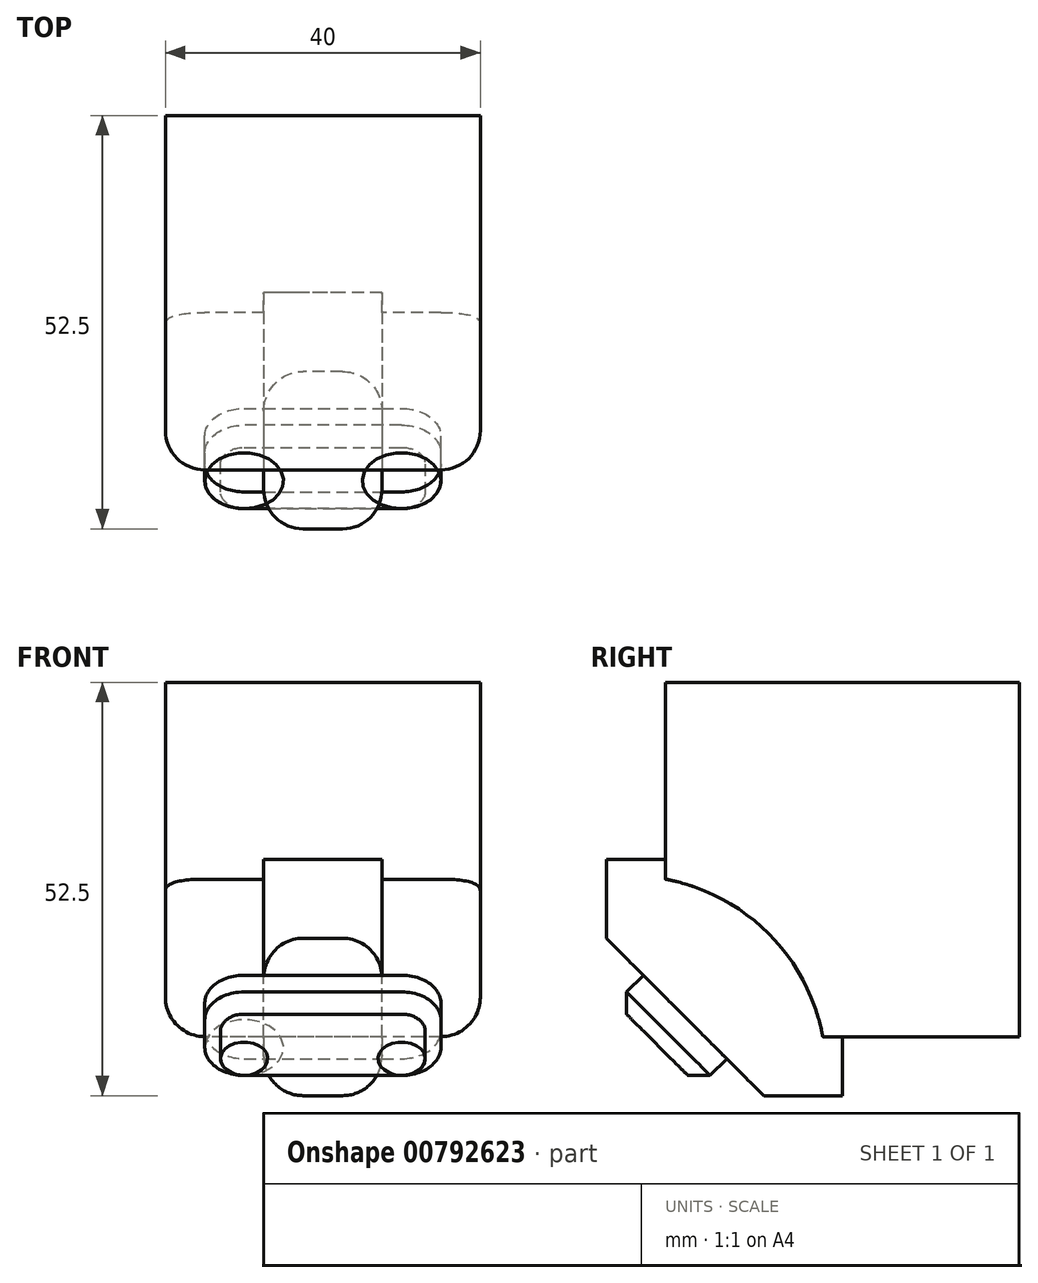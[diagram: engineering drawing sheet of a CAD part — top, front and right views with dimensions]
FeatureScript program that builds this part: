
annotation { "Feature Type Name" : "Feature", "Feature Type Description" : "" }
export const myFeature = defineFeature(function(context is Context, id is Id, definition is map)
    precondition{}
    {
        {
            var Q0;
            Q0=qCreatedBy(makeId("Top.planeOp"),FACE);
            var sketch = newSketch(context, id + "F0", { "sketchPlane" : qUnion([Q0])});
            skLineSegment(sketch, "E0.bottom", {"start": v(20, -22.5) * mm, "end": v(-20, -22.5) * mm});
            skLineSegment(sketch, "E0.top", {"start": v(20, 22.5) * mm, "end": v(-20, 22.5) * mm});
            skLineSegment(sketch, "E0.left", {"start": v(20, -22.5) * mm, "end": v(20, 22.5) * mm});
            skLineSegment(sketch, "E0.right", {"start": v(-20, -22.5) * mm, "end": v(-20, 22.5) * mm});
            skPoint(sketch, "E0.middle", {"position": v(0, 0) * mm});
            skSolve(sketch);
        }
        {
            var Q0;
            Q0=makeQuery(id+"F0.imprint","IMPRINT",FACE,{"disambiguationData":[TD([[makeQuery(id+"F0.imprint","IMPRINT",EDGE,{"derivedFrom":sQuery(id+"F0.wireOp",EDGE,"E0.bottom")}),-1.0]])]});
            extrude(context, id + "F1", {"entities" : qUnion([Q0]), "endBound" : BoundingType.SYMMETRIC, "depth" : 45 * mm, "offsetDistance" : 25 * mm});
        }
        {
            var Q0;
            Q0=makeQuery(id+"F1.opExtrude","SWEPT_FACE",FACE,{"disambiguationData":[OSD([sQuery(id+"F0.wireOp",EDGE,"E0.right")])]});
            var sketch = newSketch(context, id + "F2", { "sketchPlane" : qUnion([Q0])});
            skLineSegment(sketch, "E1", {"start": v(22.5, -22.5) * mm, "end": v(2.5, -22.5) * mm});
            skLineSegment(sketch, "E2", {"start": v(22.5, -22.5) * mm, "end": v(22.5, -2.5) * mm});
            skArc(sketch, "E3", {"start": v(22.5, -2.5) * mm, "mid": v(9.4, -9.4) * mm, "end": v(2.5, -22.5) * mm});
            skSolve(sketch);
        }
        {
            var Q0;
            Q0 = qSketchRegion(id + "F2", true);
            extrude(context, id + "F3", {"entities" : qUnion([Q0]), "operationType" : NewBodyOperationType.REMOVE, "endBound" : BoundingType.THROUGH_ALL, "oppositeDirection" : true, "depth" : 25 * mm, "offsetDistance" : 25 * mm});
        }
        {
            var Q0;
            Q0=qCreatedBy(makeId("Right.planeOp"),FACE);
            var sketch = newSketch(context, id + "F4", { "sketchPlane" : qUnion([Q0])});
            skLineSegment(sketch, "E4", {"start": v(0, 0) * mm, "end": v(-30, 0) * mm});
            skLineSegment(sketch, "E5", {"start": v(0, 0) * mm, "end": v(0, -30) * mm});
            skLineSegment(sketch, "E6", {"start": v(0, -30) * mm, "end": v(-10, -30) * mm});
            skLineSegment(sketch, "E7", {"start": v(-30, 0) * mm, "end": v(-30, -10) * mm});
            skLineSegment(sketch, "E8", {"start": v(-10, -30) * mm, "end": v(-30, -10) * mm});
            skSolve(sketch);
        }
        {
            var Q0;
            Q0 = qSketchRegion(id + "F4", true);
            extrude(context, id + "F5", {"entities" : qUnion([Q0]), "operationType" : NewBodyOperationType.ADD, "endBound" : BoundingType.SYMMETRIC, "depth" : 15 * mm, "offsetDistance" : 25 * mm});
        }
        {
            var Q0;
            Q0=makeQuery(id+"F1.opExtrude","SWEPT_EDGE",EDGE,{"disambiguationData":[OSD([sQuery(id+"F0.wireOp",EDGE,"E0.bottom"),sQuery(id+"F0.wireOp",EDGE,"E0.right")])]});
            var Q1;
            Q1=makeQuery(id+"F1.opExtrude","SWEPT_EDGE",EDGE,{"disambiguationData":[OSD([sQuery(id+"F0.wireOp",EDGE,"E0.bottom"),sQuery(id+"F0.wireOp",EDGE,"E0.left")])]});
            var Q2;
            Q2=makeQuery(id+"F1.opExtrude","CAP_EDGE",EDGE,{"disambiguationData":[OSD([sQuery(id+"F0.wireOp",EDGE,"E0.right")])],"isStart":true});
            var Q3;
            Q3=makeQuery(id+"F1.opExtrude","CAP_EDGE",EDGE,{"disambiguationData":[OSD([sQuery(id+"F0.wireOp",EDGE,"E0.left")])],"isStart":true});
            var Q4;
            Q4=makeQuery(id+"F5.opExtrude","CAP_EDGE",EDGE,{"disambiguationData":[OSD([sQuery(id+"F4.wireOp",EDGE,"E7")])],"isStart":false});
            var Q5;
            Q5=makeQuery(id+"F5.opExtrude","CAP_EDGE",EDGE,{"disambiguationData":[OSD([sQuery(id+"F4.wireOp",EDGE,"E7")])],"isStart":true});
            var Q6;
            Q6=makeQuery(id+"F5.opExtrude","CAP_EDGE",EDGE,{"disambiguationData":[OSD([sQuery(id+"F4.wireOp",EDGE,"E6")])],"isStart":false});
            var Q7;
            Q7=makeQuery(id+"F5.opExtrude","CAP_EDGE",EDGE,{"disambiguationData":[OSD([sQuery(id+"F4.wireOp",EDGE,"E6")])],"isStart":true});
            fillet(context, id + "F6", {"entities" : qUnion([Q0, Q1, Q2, Q3, Q4, Q5, Q6, Q7]), "radius" : 5 * mm, "tangentPropagation" : true, "allowEdgeOverflow" : false});
        }
        {
            var Q0;
            Q0=makeQuery(id+"F5.opExtrude","SWEPT_FACE",FACE,{"disambiguationData":[OSD([sQuery(id+"F4.wireOp",EDGE,"E8")])]});
            var sketch = newSketch(context, id + "F7", { "sketchPlane" : qUnion([Q0])});
            skLineSegment(sketch, "E9.bottom", {"start": v(-15, 7.5) * mm, "end": v(15, 7.5) * mm});
            skLineSegment(sketch, "E9.top", {"start": v(-15, -7.5) * mm, "end": v(15, -7.5) * mm});
            skLineSegment(sketch, "E9.left", {"start": v(-15, 7.5) * mm, "end": v(-15, -7.5) * mm});
            skLineSegment(sketch, "E9.right", {"start": v(15, 7.5) * mm, "end": v(15, -7.5) * mm});
            skPoint(sketch, "E9.middle", {"position": v(0, 0) * mm});
            skSolve(sketch);
        }
        {
            var Q0;
            Q0 = qSketchRegion(id + "F7", true);
            extrude(context, id + "F8", {"entities" : qUnion([Q0]), "operationType" : NewBodyOperationType.ADD, "depth" : 5 * mm, "offsetDistance" : 25 * mm});
        }
        {
            var Q0;
            Q0=makeQuery(id+"F8.opExtrude","SWEPT_EDGE",EDGE,{"disambiguationData":[OSD([sQuery(id+"F7.wireOp",EDGE,"E9.bottom"),sQuery(id+"F7.wireOp",EDGE,"E9.left")])]});
            var Q1;
            Q1=makeQuery(id+"F8.opExtrude","SWEPT_EDGE",EDGE,{"disambiguationData":[OSD([sQuery(id+"F7.wireOp",EDGE,"E9.top"),sQuery(id+"F7.wireOp",EDGE,"E9.left")])]});
            var Q2;
            Q2=makeQuery(id+"F8.opExtrude","SWEPT_EDGE",EDGE,{"disambiguationData":[OSD([sQuery(id+"F7.wireOp",EDGE,"E9.top"),sQuery(id+"F7.wireOp",EDGE,"E9.right")])]});
            var Q3;
            Q3=makeQuery(id+"F8.opExtrude","SWEPT_EDGE",EDGE,{"disambiguationData":[OSD([sQuery(id+"F7.wireOp",EDGE,"E9.bottom"),sQuery(id+"F7.wireOp",EDGE,"E9.right")])]});
            fillet(context, id + "F9", {"entities" : qUnion([Q0, Q1, Q2, Q3]), "radius" : 5 * mm, "tangentPropagation" : true, "allowEdgeOverflow" : false});
        }
        {
            var Q0;
            Q0=makeQuery(id+"F8.opExtrude","CAP_EDGE",EDGE,{"disambiguationData":[OSD([sQuery(id+"F7.wireOp",EDGE,"E9.top")])],"isStart":false});
            chamfer(context, id + "F10", {"entities" : qUnion([Q0]), "width" : 2 * mm, "tangentPropagation" : true});
        }
    });
